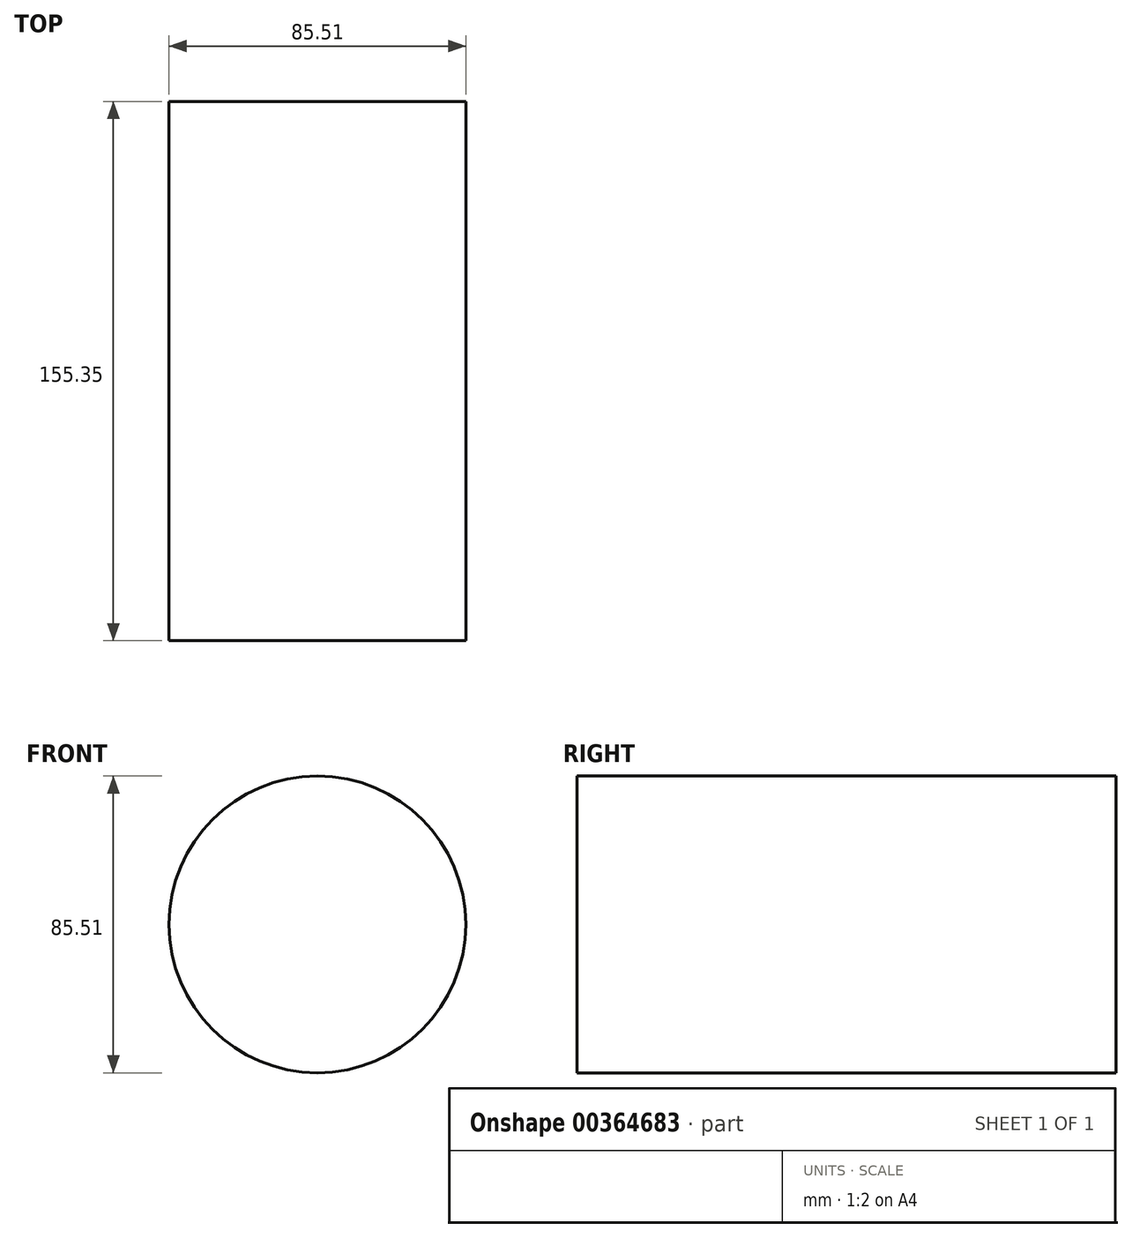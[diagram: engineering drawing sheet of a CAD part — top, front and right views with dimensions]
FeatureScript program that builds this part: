
annotation { "Feature Type Name" : "Feature", "Feature Type Description" : "" }
export const myFeature = defineFeature(function(context is Context, id is Id, definition is map)
    precondition{}
    {
        {
            var Q0;
            Q0=qCreatedBy(makeId("Front.planeOp"),FACE);
            var sketch = newSketch(context, id + "F0", { "sketchPlane" : qUnion([Q0])});
            skCircle(sketch, "E0", {"center": v(-40.22, 38.76) * mm, "radius": 42.76 * mm});
            skPoint(sketch, "E0.first.point", {"position": v(-58.26, 0) * mm});
            skPoint(sketch, "E0.second.point", {"position": v(0, 53.27) * mm});
            skPoint(sketch, "E0.third.point", {"position": v(-51.21, 80.08) * mm});
            skCircle(sketch, "E1.cCircle", {"center": v(33.17, 49.67) * mm, "radius": 35.47 * mm, "construction": true});
            skLineSegment(sketch, "E1.0", {"start": v(41.93, 15.3) * mm, "end": v(-0.98, 59.26) * mm, "construction": true});
            skLineSegment(sketch, "E1.1", {"start": v(-0.98, 59.26) * mm, "end": v(58.55, 74.44) * mm, "construction": true});
            skLineSegment(sketch, "E1.2", {"start": v(58.55, 74.44) * mm, "end": v(41.93, 15.3) * mm, "construction": true});
            skSolve(sketch);
        }
        {
            var Q0;
            Q0=makeQuery(id+"F0.imprint","IMPRINT",FACE,{"disambiguationData":[TD([[makeQuery(id+"F0.imprint","IMPRINT",EDGE,{"derivedFrom":sQuery(id+"F0.wireOp",EDGE,"E0")}),1.0]])]});
            var Q1;
            Q1=sQuery(id+"F0.wireOp",EDGE,"E0");
            extrude(context, id + "F1", {"entities" : qUnion([Q0]), "surfaceEntities" : qUnion([Q1]), "depth" : 155.35 * mm});
        }
    });
